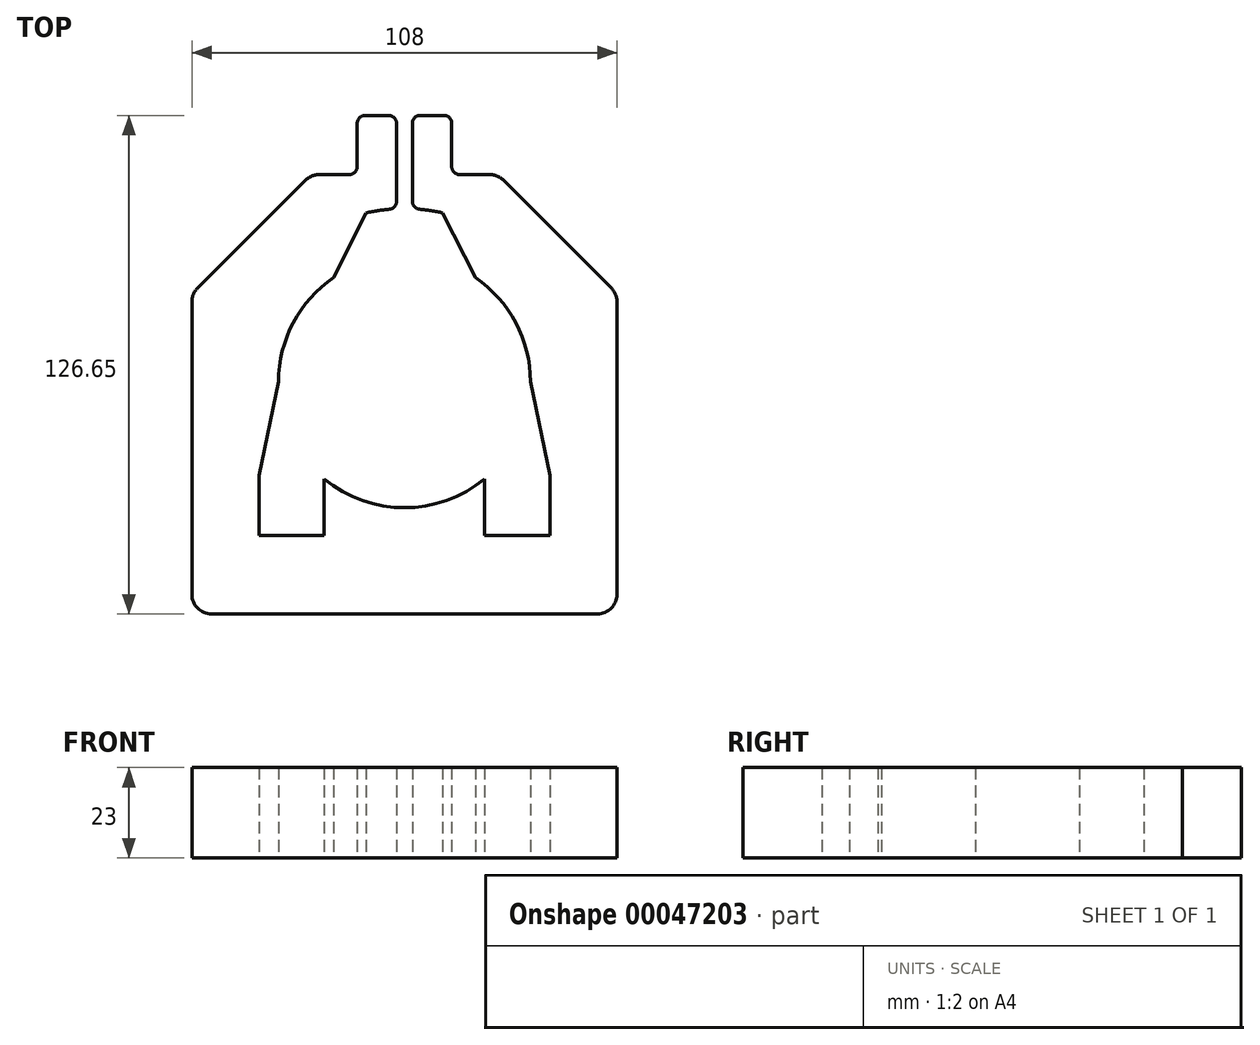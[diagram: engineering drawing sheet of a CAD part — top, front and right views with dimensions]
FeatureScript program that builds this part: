
annotation { "Feature Type Name" : "Feature", "Feature Type Description" : "" }
export const myFeature = defineFeature(function(context is Context, id is Id, definition is map)
    precondition{}
    {
        {
            var Q0;
            Q0=qCreatedBy(makeId("Top.planeOp"),FACE);
            var sketch = newSketch(context, id + "F0", { "sketchPlane" : qUnion([Q0])});
            skArc(sketch, "E0", {"start": v(-3.83, 43.83) * mm, "mid": v(-39.5, 19.37) * mm, "end": v(-37, -23.81) * mm});
            skLineSegment(sketch, "E1.bottom", {"start": v(-10, 67.65) * mm, "end": v(-4, 67.65) * mm});
            skLineSegment(sketch, "E1.top", {"start": v(-49, -59) * mm, "end": v(49, -59) * mm});
            skLineSegment(sketch, "E1.left", {"start": v(-54, 20.3) * mm, "end": v(-54, -54) * mm});
            skLineSegment(sketch, "E1.right", {"start": v(54, 20.3) * mm, "end": v(54, -54) * mm});
            skLineSegment(sketch, "E2", {"start": v(-12, 65.65) * mm, "end": v(-12, 54.65) * mm});
            skLineSegment(sketch, "E3", {"start": v(-14, 52.65) * mm, "end": v(-21.65, 52.65) * mm});
            skLineSegment(sketch, "E4", {"start": v(-25.18, 51.19) * mm, "end": v(-52.54, 23.83) * mm});
            skLineSegment(sketch, "E5.MirrorCS", {"start": v(12, 65.65) * mm, "end": v(12, 54.65) * mm});
            skLineSegment(sketch, "E6.MirrorCS", {"start": v(14, 52.65) * mm, "end": v(21.65, 52.65) * mm});
            skLineSegment(sketch, "E7.MirrorCS", {"start": v(25.18, 51.19) * mm, "end": v(52.54, 23.83) * mm});
            skLineSegment(sketch, "E8", {"start": v(-2, 65.65) * mm, "end": v(-2, 45.83) * mm});
            skLineSegment(sketch, "E9.MirrorCS", {"start": v(2, 65.65) * mm, "end": v(2, 45.83) * mm});
            skLineSegment(sketch, "E10.trimOffspring", {"start": v(4, 67.65) * mm, "end": v(10, 67.65) * mm});
            skLineSegment(sketch, "E11.top", {"start": v(-37, -39) * mm, "end": v(-20.37, -39) * mm});
            skLineSegment(sketch, "E11.left", {"start": v(-37, -23.81) * mm, "end": v(-37, -39) * mm});
            skLineSegment(sketch, "E11.right", {"start": v(37, -23.81) * mm, "end": v(37, -39) * mm});
            skArc(sketch, "E12.trimOffspring", {"start": v(-20.37, -39) * mm, "mid": v(0, -44) * mm, "end": v(20.37, -39) * mm});
            skArc(sketch, "E13.trimOffspring", {"start": v(37, -23.81) * mm, "mid": v(39.5, 19.37) * mm, "end": v(3.83, 43.83) * mm});
            skLineSegment(sketch, "E14.trimOffspring", {"start": v(20.37, -39) * mm, "end": v(37, -39) * mm});
            skPoint(sketch, "E15.visualSharp", {"position": v(-54, 22.37) * mm});
            skArc(sketch, "E15.filletArc", {"start": v(-52.54, 23.83) * mm, "mid": v(-53.62, 22.2) * mm, "end": v(-54, 20.3) * mm});
            skPoint(sketch, "E16.visualSharp", {"position": v(54, 22.37) * mm});
            skArc(sketch, "E16.filletArc", {"start": v(54, 20.3) * mm, "mid": v(53.62, 22.2) * mm, "end": v(52.54, 23.83) * mm});
            skPoint(sketch, "E17.visualSharp", {"position": v(54, -59) * mm});
            skArc(sketch, "E17.filletArc", {"start": v(49, -59) * mm, "mid": v(52.54, -57.54) * mm, "end": v(54, -54) * mm});
            skPoint(sketch, "E18.visualSharp", {"position": v(-54, -59) * mm});
            skArc(sketch, "E18.filletArc", {"start": v(-54, -54) * mm, "mid": v(-52.54, -57.54) * mm, "end": v(-49, -59) * mm});
            skPoint(sketch, "E19.visualSharp", {"position": v(-23.72, 52.65) * mm});
            skArc(sketch, "E19.filletArc", {"start": v(-21.65, 52.65) * mm, "mid": v(-23.56, 52.27) * mm, "end": v(-25.18, 51.19) * mm});
            skPoint(sketch, "E20.visualSharp", {"position": v(23.72, 52.65) * mm});
            skArc(sketch, "E20.filletArc", {"start": v(25.18, 51.19) * mm, "mid": v(23.56, 52.27) * mm, "end": v(21.65, 52.65) * mm});
            skPoint(sketch, "E21.visualSharp", {"position": v(12, 67.65) * mm});
            skArc(sketch, "E21.filletArc", {"start": v(12, 65.65) * mm, "mid": v(11.41, 67.06) * mm, "end": v(10, 67.65) * mm});
            skPoint(sketch, "E22.visualSharp", {"position": v(12, 52.65) * mm});
            skArc(sketch, "E22.filletArc", {"start": v(12, 54.65) * mm, "mid": v(12.59, 53.24) * mm, "end": v(14, 52.65) * mm});
            skPoint(sketch, "E23.visualSharp", {"position": v(2, 67.65) * mm});
            skArc(sketch, "E23.filletArc", {"start": v(4, 67.65) * mm, "mid": v(2.59, 67.06) * mm, "end": v(2, 65.65) * mm});
            skPoint(sketch, "E24.visualSharp", {"position": v(-2, 67.65) * mm});
            skArc(sketch, "E24.filletArc", {"start": v(-2, 65.65) * mm, "mid": v(-2.59, 67.06) * mm, "end": v(-4, 67.65) * mm});
            skPoint(sketch, "E25.visualSharp", {"position": v(-12, 67.65) * mm});
            skArc(sketch, "E25.filletArc", {"start": v(-10, 67.65) * mm, "mid": v(-11.41, 67.06) * mm, "end": v(-12, 65.65) * mm});
            skPoint(sketch, "E26.visualSharp", {"position": v(-12, 52.65) * mm});
            skArc(sketch, "E26.filletArc", {"start": v(-14, 52.65) * mm, "mid": v(-12.59, 53.24) * mm, "end": v(-12, 54.65) * mm});
            skPoint(sketch, "E27.visualSharp", {"position": v(-2, 43.95) * mm});
            skArc(sketch, "E27.filletArc", {"start": v(-3.83, 43.83) * mm, "mid": v(-2.53, 44.47) * mm, "end": v(-2, 45.83) * mm});
            skPoint(sketch, "E28.visualSharp", {"position": v(2, 43.95) * mm});
            skArc(sketch, "E28.filletArc", {"start": v(2, 45.83) * mm, "mid": v(2.53, 44.47) * mm, "end": v(3.83, 43.83) * mm});
            skCircle(sketch, "E29", {"center": v(0, 0) * mm, "radius": 32 * mm});
            skLineSegment(sketch, "E30", {"start": v(-20.37, -39) * mm, "end": v(-20.37, -24.68) * mm});
            skLineSegment(sketch, "E31", {"start": v(20.37, -39) * mm, "end": v(20.37, -24.68) * mm});
            skPoint(sketch, "E32", {"position": v(0, -59) * mm});
            skLineSegment(sketch, "E33", {"start": v(-44, 0) * mm, "end": v(-32, 0) * mm});
            skLineSegment(sketch, "E34", {"start": v(32, 0) * mm, "end": v(44, 0) * mm});
            skLineSegment(sketch, "E35", {"start": v(-18, 26.46) * mm, "end": v(-25, 36.21) * mm});
            skLineSegment(sketch, "E36.MirrorCS", {"start": v(18, 26.46) * mm, "end": v(25, 36.21) * mm});
            skLineSegment(sketch, "E37", {"start": v(-37, -23.81) * mm, "end": v(-32, 0) * mm});
            skLineSegment(sketch, "E38", {"start": v(37, -23.81) * mm, "end": v(32, 0) * mm});
            skLineSegment(sketch, "E39", {"start": v(-18, 26.46) * mm, "end": v(-9.71, 42.91) * mm});
            skLineSegment(sketch, "E40.MirrorCS", {"start": v(18, 26.46) * mm, "end": v(9.71, 42.91) * mm});
            skLineSegment(sketch, "E41", {"start": v(-30, -28.88) * mm, "end": v(-30, -71.93) * mm, "construction": true});
            skSolve(sketch);
        }
        {
            var Q0;
            Q0=makeQuery(id+"F0.imprint","IMPRINT",FACE,{"disambiguationData":[TD([[makeQuery(id+"F0.imprint","IMPRINT",EDGE,{"derivedFrom":sQuery(id+"F0.wireOp",EDGE,"E0")}),-1.0]])]});
            var Q1;
            {var subQ0=sQuery(id+"F0.wireOp",EDGE,"E33");Q1=makeQuery(id+"F0.imprint","IMPRINT",FACE,{"disambiguationData":[TD([[makeQuery(id+"F0.imprint","IMPRINT",EDGE,{"derivedFrom":subQ0}),1.0]])]});}
            var Q2;
            Q2=makeQuery(id+"F0.imprint","IMPRINT",FACE,{"disambiguationData":[TD([[makeQuery(id+"F0.imprint","IMPRINT",EDGE,{"derivedFrom":sQuery(id+"F0.wireOp",EDGE,"E12.trimOffspring")}),1.0]])]});
            var Q3;
            {var subQ0=sQuery(id+"F0.wireOp",EDGE,"E34");Q3=makeQuery(id+"F0.imprint","IMPRINT",FACE,{"disambiguationData":[TD([[makeQuery(id+"F0.imprint","IMPRINT",EDGE,{"derivedFrom":subQ0}),1.0]])]});}
            var Q4;
            {var subQ2=sQuery(id+"F0.wireOp",EDGE,"E33");Q4=makeQuery(id+"F0.imprint","IMPRINT",FACE,{"disambiguationData":[TD([[makeQuery(id+"F0.imprint","IMPRINT",EDGE,{"derivedFrom":subQ2}),-1.0]])]});}
            var Q5;
            {var subQ2=sQuery(id+"F0.wireOp",EDGE,"E34");Q5=makeQuery(id+"F0.imprint","IMPRINT",FACE,{"disambiguationData":[TD([[makeQuery(id+"F0.imprint","IMPRINT",EDGE,{"derivedFrom":subQ2}),-1.0]])]});}
            var Q6;
            {var subQ0=sQuery(id+"F0.wireOp",EDGE,"E35");Q6=makeQuery(id+"F0.imprint","IMPRINT",FACE,{"disambiguationData":[TD([[makeQuery(id+"F0.imprint","IMPRINT",EDGE,{"derivedFrom":subQ0}),-1.0]])]});}
            var Q7;
            {var subQ0=sQuery(id+"F0.wireOp",EDGE,"E36.MirrorCS");Q7=makeQuery(id+"F0.imprint","IMPRINT",FACE,{"disambiguationData":[TD([[makeQuery(id+"F0.imprint","IMPRINT",EDGE,{"derivedFrom":subQ0}),1.0]])]});}
            extrude(context, id + "F1", {"entities" : qUnion([Q0, Q1, Q2, Q3, Q4, Q5, Q6, Q7]), "depth" : 23 * mm});
        }
    });
